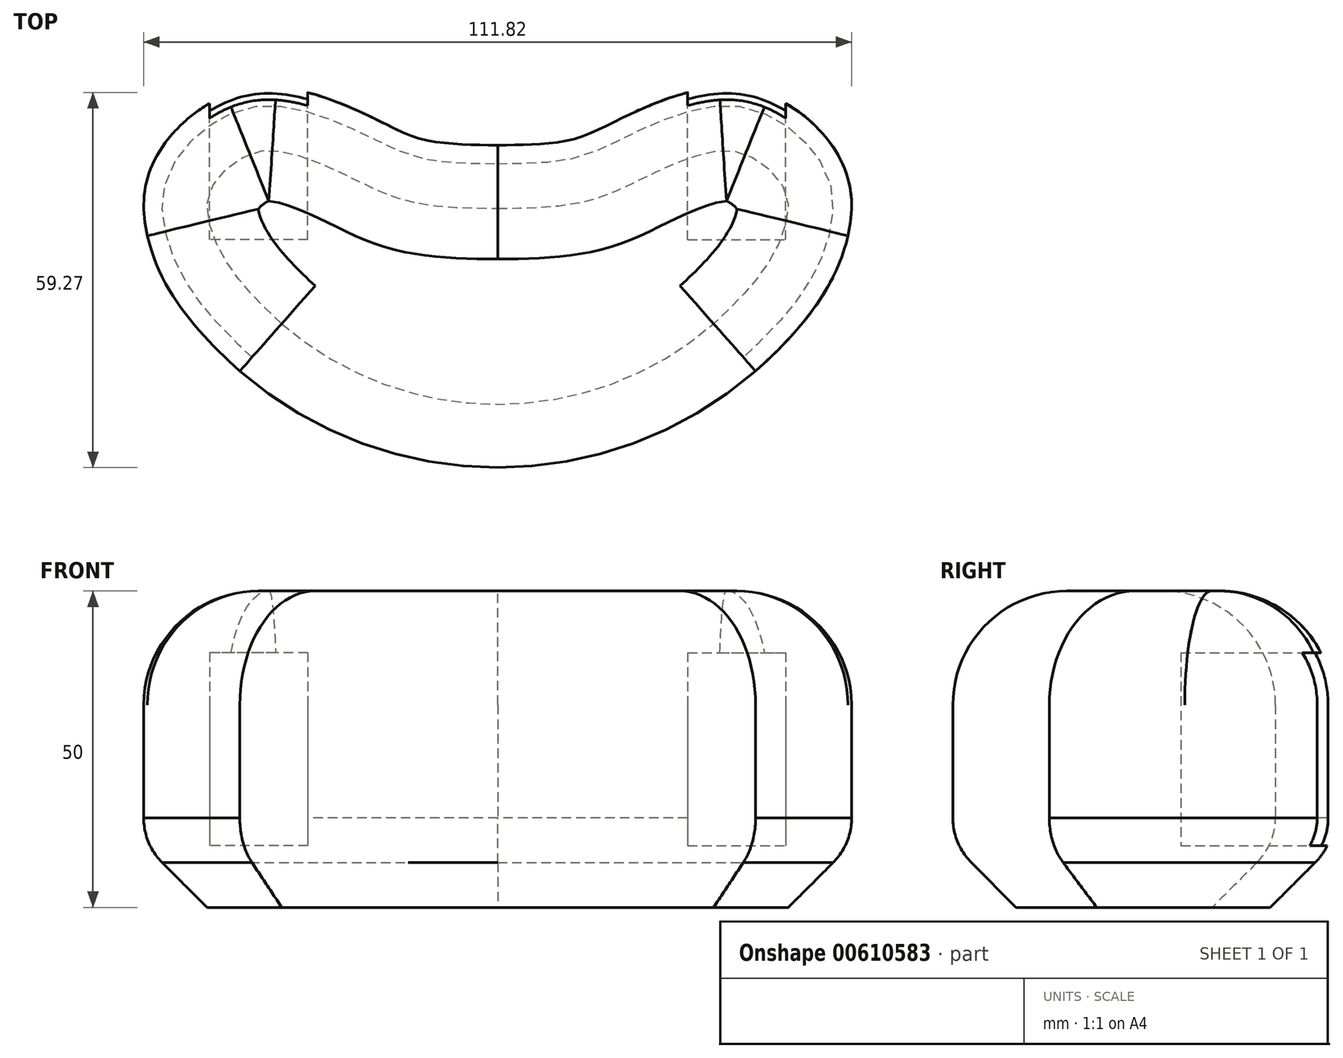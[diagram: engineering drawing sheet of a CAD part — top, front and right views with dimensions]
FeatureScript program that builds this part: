
annotation { "Feature Type Name" : "Feature", "Feature Type Description" : "" }
export const myFeature = defineFeature(function(context is Context, id is Id, definition is map)
    precondition{}
    {
        {
            var Q0;
            Q0=qCreatedBy(makeId("Top.planeOp"),FACE);
            var sketch = newSketch(context, id + "F0", { "sketchPlane" : qUnion([Q0])});
            skArc(sketch, "E0", {"start": v(-40.74, 15.23) * mm, "mid": v(-21.74, 3.93) * mm, "end": v(0, 0) * mm});
            skArc(sketch, "E1.MirrorCS", {"start": v(40.74, 15.23) * mm, "mid": v(21.74, 3.93) * mm, "end": v(0, 0) * mm});
            skFitSpline(sketch, "E2", {"points": [v(-40.74, 15.23) * mm, v(-55, 35.32) * mm, v(-54.13, 48.7) * mm, v(-37.82, 60.06) * mm, v(-16.78, 53.83) * mm, v(0, 50.95) * mm], "startDerivative": vector(-115.58, 104.02) * mm, "endDerivative": vector(168, -1.4) * mm});
            skFitSpline(sketch, "E3.MirrorCS", {"points": [v(40.74, 15.23) * mm, v(55, 35.32) * mm, v(54.13, 48.7) * mm, v(37.82, 60.06) * mm, v(16.78, 53.83) * mm, v(0, 50.95) * mm], "startDerivative": vector(115.58, 104.02) * mm, "endDerivative": vector(-168, -1.4) * mm});
            skSolve(sketch);
        }
        {
            var Q0;
            Q0=makeQuery(id+"F0.imprint","IMPRINT",FACE,{"disambiguationData":[TD([[makeQuery(id+"F0.imprint","IMPRINT",EDGE,{"derivedFrom":sQuery(id+"F0.wireOp",EDGE,"E0")}),1.0]])]});
            extrude(context, id + "F1", {"entities" : qUnion([Q0]), "endBound" : BoundingType.SYMMETRIC, "depth" : 50 * mm, "offsetDistance" : 25 * mm});
        }
        {
            var Q0;
            Q0=makeQuery(id+"F1.opExtrude","CAP_FACE",FACE,{"disambiguationData":[OSD([sQuery(id+"F0.wireOp",EDGE,"E0"),sQuery(id+"F0.wireOp",EDGE,"E1.MirrorCS"),sQuery(id+"F0.wireOp",EDGE,"E2"),sQuery(id+"F0.wireOp",EDGE,"E3.MirrorCS")])],"isStart":false});
            fillet(context, id + "F2", {"entities" : qUnion([Q0]), "radius" : 18 * mm, "tangentPropagation" : true, "allowEdgeOverflow" : false});
        }
        {
            var Q0;
            Q0=makeQuery(id+"F1.opExtrude","CAP_FACE",FACE,{"disambiguationData":[OSD([sQuery(id+"F0.wireOp",EDGE,"E0"),sQuery(id+"F0.wireOp",EDGE,"E1.MirrorCS"),sQuery(id+"F0.wireOp",EDGE,"E2"),sQuery(id+"F0.wireOp",EDGE,"E3.MirrorCS")])],"isStart":true});
            chamfer(context, id + "F3", {"entities" : qUnion([Q0]), "width" : 10 * mm, "tangentPropagation" : true});
        }
        {
            var Q0;
            {var subQ0=sQuery(id+"F0.wireOp",EDGE,"E3.MirrorCS");Q0=makeQuery(id+"F3.opChamfer","BLEND_EDGE",EDGE,{"blendedFrom":[makeQuery(id+"F1.opExtrude","CAP_EDGE",EDGE,{"disambiguationData":[OSD([subQ0])],"isStart":true}),makeQuery(id+"F1.opExtrude","SWEPT_FACE",FACE,{"disambiguationData":[OSD([subQ0])]})],"blendedInto":[makeQuery(id+"F1.opExtrude","SWEPT_FACE",FACE,{"disambiguationData":[OSD([subQ0])]})]});}
            var Q1;
            {var subQ0=sQuery(id+"F0.wireOp",EDGE,"E2");Q1=makeQuery(id+"F3.opChamfer","BLEND_EDGE",EDGE,{"blendedFrom":[makeQuery(id+"F1.opExtrude","CAP_EDGE",EDGE,{"disambiguationData":[OSD([subQ0])],"isStart":true}),makeQuery(id+"F1.opExtrude","SWEPT_FACE",FACE,{"disambiguationData":[OSD([subQ0])]})],"blendedInto":[makeQuery(id+"F1.opExtrude","SWEPT_FACE",FACE,{"disambiguationData":[OSD([subQ0])]})]});}
            var Q2;
            {var subQ0=sQuery(id+"F0.wireOp",EDGE,"E1.MirrorCS");var subQ1=sQuery(id+"F0.wireOp",EDGE,"E0");Q2=makeQuery(id+"F3.opChamfer","BLEND_EDGE",EDGE,{"blendedFrom":[makeQuery(id+"F1.opExtrude","CAP_EDGE",EDGE,{"disambiguationData":[OSD([subQ1,subQ0])],"isStart":true}),makeQuery(id+"F1.opExtrude","SWEPT_FACE",FACE,{"disambiguationData":[OSD([subQ1,subQ0])]})],"blendedInto":[makeQuery(id+"F1.opExtrude","SWEPT_FACE",FACE,{"disambiguationData":[OSD([subQ1,subQ0])]})]});}
            fillet(context, id + "F4", {"entities" : qUnion([Q0, Q1, Q2]), "radius" : 10 * mm, "tangentPropagation" : true, "allowEdgeOverflow" : false});
        }
        {
            var Q0;
            Q0=qCreatedBy(makeId("Front.planeOp"),FACE);
            cPlane(context, id + "F5", {"entities" : qUnion([Q0]), "cplaneType" : CPlaneType.OFFSET, "offset" : 61 * mm, "oppositeDirection" : true, "width" : 150 * mm, "height" : 150 * mm});
        }
        {
            var Q0;
            Q0=qCreatedBy(id+"F5.planeOp",FACE);
            var sketch = newSketch(context, id + "F6", { "sketchPlane" : qUnion([Q0])});
            skLineSegment(sketch, "E4.bottom", {"start": v(30, 15.25) * mm, "end": v(45.5, 15.25) * mm});
            skLineSegment(sketch, "E4.top", {"start": v(30, -15.25) * mm, "end": v(45.5, -15.25) * mm});
            skLineSegment(sketch, "E4.left", {"start": v(30, 15.25) * mm, "end": v(30, -15.25) * mm});
            skLineSegment(sketch, "E4.right", {"start": v(45.5, 15.25) * mm, "end": v(45.5, -15.25) * mm});
            skPoint(sketch, "E4.middle", {"position": v(37.75, 0) * mm});
            skLineSegment(sketch, "E5.MirrorCS", {"start": v(-30, 15.25) * mm, "end": v(-45.5, 15.25) * mm});
            skLineSegment(sketch, "E6.MirrorCS", {"start": v(-30, 15.25) * mm, "end": v(-30, -15.25) * mm});
            skLineSegment(sketch, "E7.MirrorCS", {"start": v(-30, -15.25) * mm, "end": v(-45.5, -15.25) * mm});
            skLineSegment(sketch, "E8.MirrorCS", {"start": v(-45.5, 15.25) * mm, "end": v(-45.5, -15.25) * mm});
            skSolve(sketch);
        }
        {
            var Q0;
            Q0=makeQuery(id+"F6.imprint","IMPRINT",FACE,{"disambiguationData":[TD([[makeQuery(id+"F6.imprint","IMPRINT",EDGE,{"derivedFrom":sQuery(id+"F6.wireOp",EDGE,"E4.bottom")}),-1.0]])]});
            var Q1;
            Q1=makeQuery(id+"F6.imprint","IMPRINT",FACE,{"disambiguationData":[TD([[makeQuery(id+"F6.imprint","IMPRINT",EDGE,{"derivedFrom":sQuery(id+"F6.wireOp",EDGE,"E5.MirrorCS")}),1.0]])]});
            extrude(context, id + "F7", {"entities" : qUnion([Q0, Q1]), "operationType" : NewBodyOperationType.REMOVE, "depth" : 25 * mm, "offsetDistance" : 25 * mm});
        }
    });
